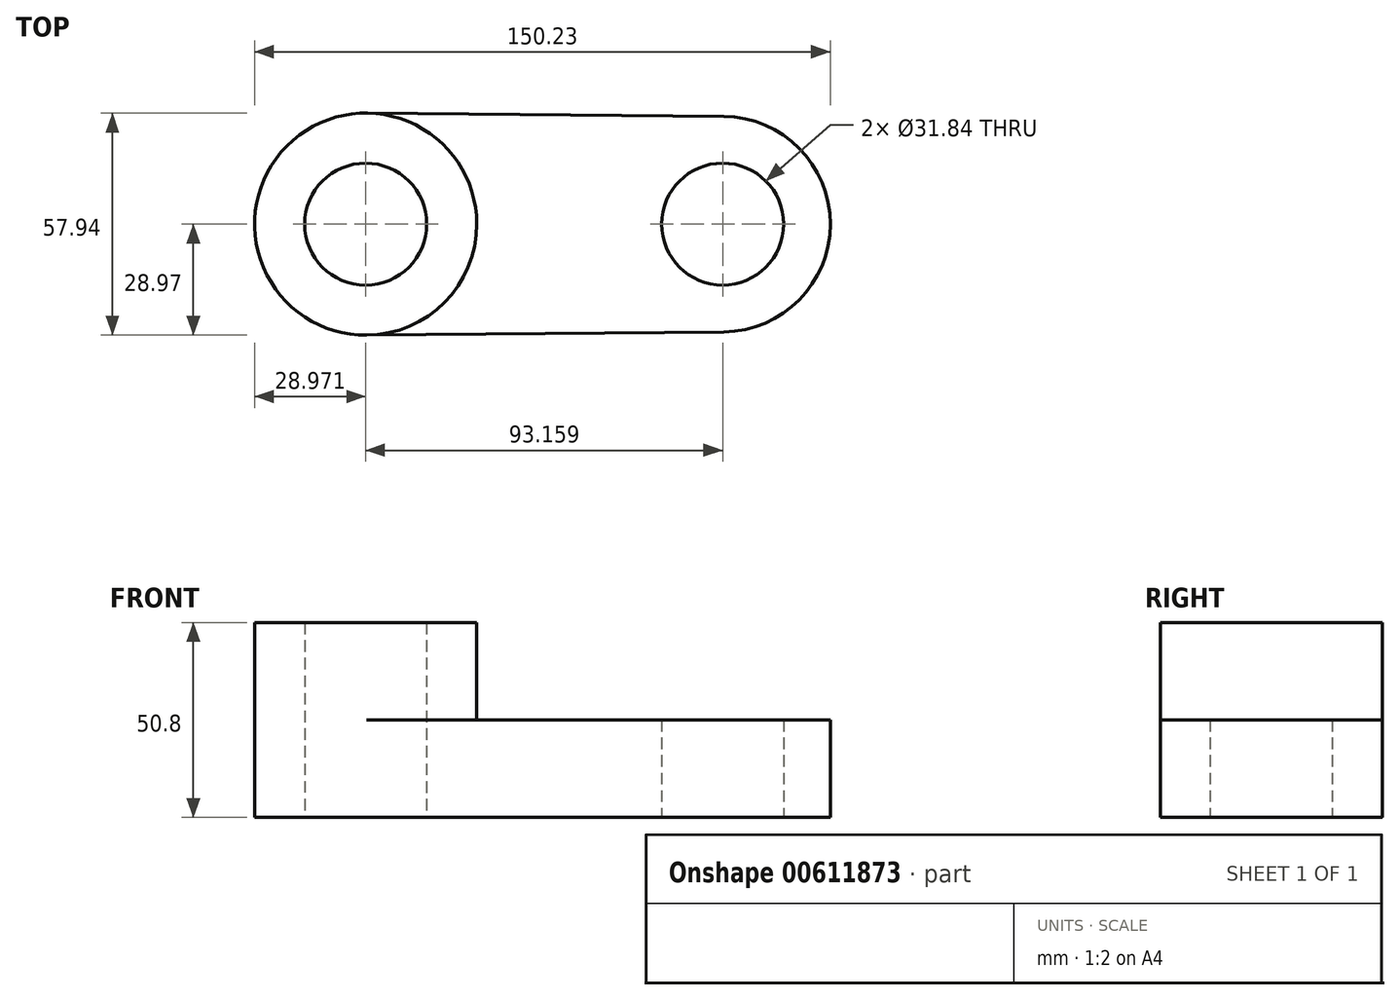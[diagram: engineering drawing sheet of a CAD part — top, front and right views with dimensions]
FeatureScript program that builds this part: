
annotation { "Feature Type Name" : "Feature", "Feature Type Description" : "" }
export const myFeature = defineFeature(function(context is Context, id is Id, definition is map)
    precondition{}
    {
        {
            var Q0;
            Q0=qCreatedBy(makeId("Top.planeOp"),FACE);
            var sketch = newSketch(context, id + "F0", { "sketchPlane" : qUnion([Q0])});
            skCircle(sketch, "E0", {"center": v(-46.58, 0) * mm, "radius": 15.92 * mm});
            skCircle(sketch, "E1", {"center": v(46.58, 0) * mm, "radius": 15.92 * mm});
            skArc(sketch, "E2", {"start": v(-46.3, 28.97) * mm, "mid": v(-75.55, 0) * mm, "end": v(-46.3, -28.97) * mm});
            skArc(sketch, "E3", {"start": v(46.84, -28.1) * mm, "mid": v(74.68, 0) * mm, "end": v(46.84, 28.1) * mm});
            skLineSegment(sketch, "E4", {"start": v(-46.3, 28.97) * mm, "end": v(46.84, 28.1) * mm});
            skLineSegment(sketch, "E5", {"start": v(46.84, -28.1) * mm, "end": v(-46.3, -28.97) * mm});
            skArc(sketch, "E6", {"start": v(-46.3, -28.97) * mm, "mid": v(-17.6, 0) * mm, "end": v(-46.3, 28.97) * mm});
            skSolve(sketch);
        }
        {
            var Q0;
            Q0=makeQuery(id+"F0.imprint","IMPRINT",FACE,{"disambiguationData":[TD([[makeQuery(id+"F0.imprint","IMPRINT",EDGE,{"derivedFrom":sQuery(id+"F0.wireOp",EDGE,"E0")}),-1.0]])]});
            extrude(context, id + "F1", {"entities" : qUnion([Q0]), "depth" : 25.4 * mm, "offsetDistance" : 25.4 * mm});
        }
        {
            var Q0;
            Q0=makeQuery(id+"F1.opExtrude","CAP_FACE",FACE,{"disambiguationData":[OSD([sQuery(id+"F0.wireOp",EDGE,"E0"),sQuery(id+"F0.wireOp",EDGE,"E2"),sQuery(id+"F0.wireOp",EDGE,"E6")])],"isStart":false});
            extrude(context, id + "F2", {"entities" : qUnion([Q0]), "operationType" : NewBodyOperationType.ADD, "depth" : 25.4 * mm, "offsetDistance" : 25.4 * mm});
        }
        {
            var Q0;
            Q0=makeQuery(id+"F0.imprint","IMPRINT",FACE,{"disambiguationData":[TD([[makeQuery(id+"F0.imprint","IMPRINT",EDGE,{"derivedFrom":sQuery(id+"F0.wireOp",EDGE,"E1")}),-1.0]])]});
            extrude(context, id + "F3", {"entities" : qUnion([Q0]), "operationType" : NewBodyOperationType.ADD, "depth" : 25.4 * mm, "offsetDistance" : 25.4 * mm});
        }
    });
